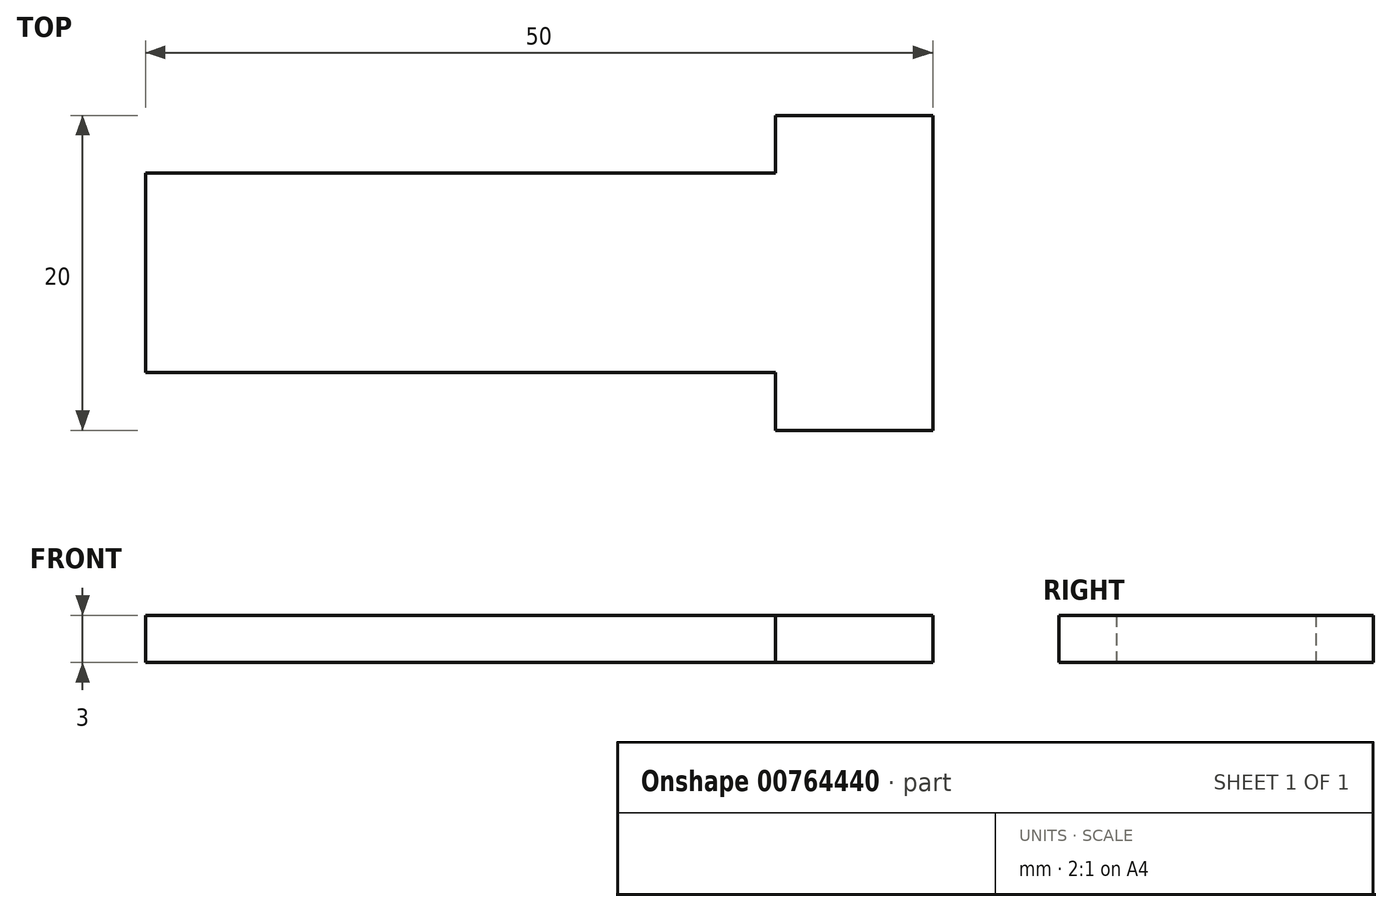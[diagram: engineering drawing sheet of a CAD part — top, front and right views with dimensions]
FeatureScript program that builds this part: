
annotation { "Feature Type Name" : "Feature", "Feature Type Description" : "" }
export const myFeature = defineFeature(function(context is Context, id is Id, definition is map)
    precondition{}
    {
        {
            var Q0;
            Q0=qCreatedBy(makeId("Top.planeOp"),FACE);
            var sketch = newSketch(context, id + "F0", { "sketchPlane" : qUnion([Q0])});
            skLineSegment(sketch, "E0.bottom", {"start": v(22.5, -6.33) * mm, "end": v(-22.5, -6.32) * mm});
            skLineSegment(sketch, "E0.top", {"start": v(22.5, 6.32) * mm, "end": v(-22.5, 6.33) * mm});
            skLineSegment(sketch, "E0.left", {"start": v(22.5, -6.32) * mm, "end": v(22.5, 6.32) * mm});
            skLineSegment(sketch, "E0.right", {"start": v(-22.5, -6.33) * mm, "end": v(-22.5, 6.33) * mm});
            skPoint(sketch, "E0.middle", {"position": v(0, 0) * mm});
            skLineSegment(sketch, "E1.bottom", {"start": v(27.5, -10) * mm, "end": v(17.5, -10) * mm});
            skLineSegment(sketch, "E1.top", {"start": v(27.5, 10) * mm, "end": v(17.5, 10) * mm});
            skLineSegment(sketch, "E1.left", {"start": v(27.5, -10) * mm, "end": v(27.5, 10) * mm});
            skLineSegment(sketch, "E1.right", {"start": v(17.5, -10) * mm, "end": v(17.5, 10) * mm});
            skPoint(sketch, "E1.middle", {"position": v(22.5, 0) * mm});
            skSolve(sketch);
        }
        {
            var Q0;
            Q0=makeQuery(id+"F0.imprint","IMPRINT",FACE,{"disambiguationData":[TD([[makeQuery(id+"F0.imprint","IMPRINT",EDGE,{"derivedFrom":sQuery(id+"F0.wireOp",EDGE,"E0.bottom")}),-1.0]])]});
            var Q1;
            {var subQ1=sQuery(id+"F0.wireOp",EDGE,"E0.left");Q1=makeQuery(id+"F0.imprint","IMPRINT",FACE,{"disambiguationData":[TD([[makeQuery(id+"F0.imprint","IMPRINT",EDGE,{"derivedFrom":subQ1}),-1.0]])]});}
            extrude(context, id + "F1", {"entities" : qUnion([Q0, Q1]), "endBound" : BoundingType.SYMMETRIC, "depth" : 3 * mm, "offsetDistance" : 25 * mm});
        }
    });
